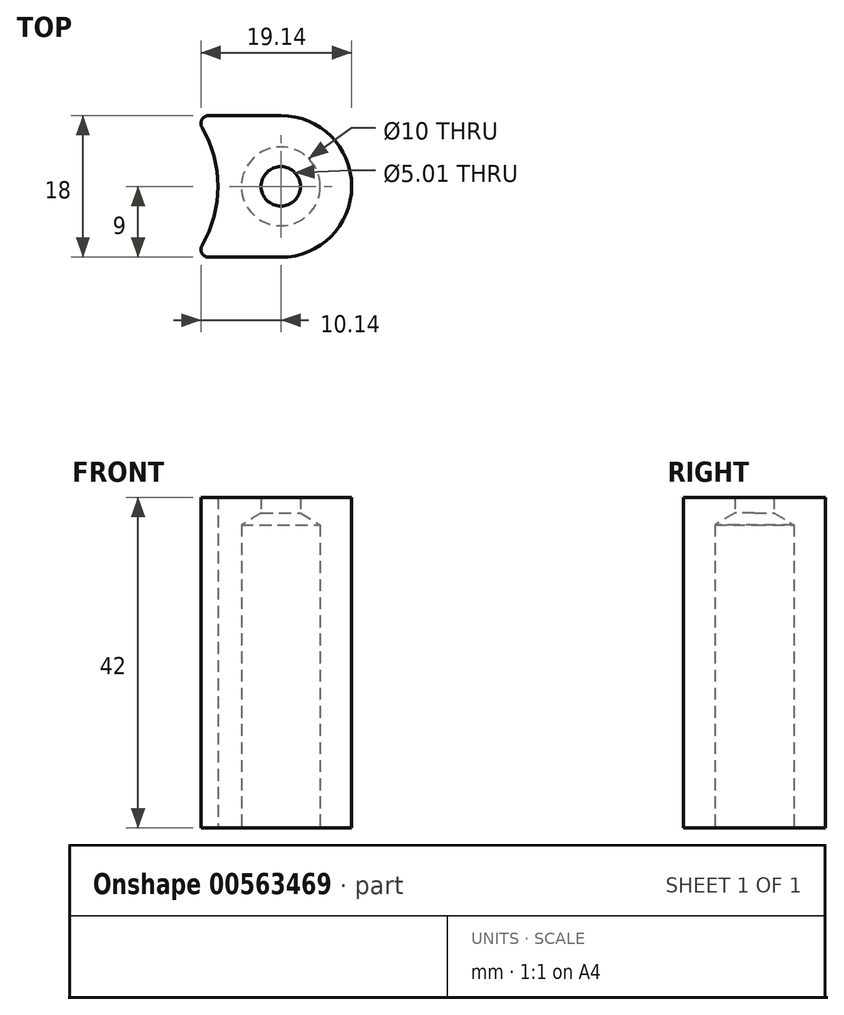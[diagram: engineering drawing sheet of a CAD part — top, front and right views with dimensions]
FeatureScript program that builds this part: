
annotation { "Feature Type Name" : "Feature", "Feature Type Description" : "" }
export const myFeature = defineFeature(function(context is Context, id is Id, definition is map)
    precondition{}
    {
        {
            var Q0;
            Q0=qCreatedBy(makeId("Top.planeOp"),FACE);
            var sketch = newSketch(context, id + "F0", { "sketchPlane" : qUnion([Q0])});
            skCircle(sketch, "E0", {"center": v(0, 0) * mm, "radius": 5 * mm});
            skCircle(sketch, "E1", {"center": v(0, 0) * mm, "radius": 9 * mm});
            skLineSegment(sketch, "E2.bottom", {"start": v(0, 9) * mm, "end": v(-11, 9) * mm});
            skLineSegment(sketch, "E2.top", {"start": v(0, -9) * mm, "end": v(-11, -9) * mm});
            skLineSegment(sketch, "E2.left", {"start": v(0, 9) * mm, "end": v(0, -9) * mm});
            skLineSegment(sketch, "E2.right", {"start": v(-11, 9) * mm, "end": v(-11, -9) * mm});
            skArc(sketch, "E3", {"start": v(-11, -9) * mm, "mid": v(-8, 0) * mm, "end": v(-11, 9) * mm});
            skSolve(sketch);
        }
        {
            var Q0;
            {var subQ0=sQuery(id+"F0.wireOp",EDGE,"E2.left");var subQ5=sQuery(id+"F0.wireOp",EDGE,"E0");var subQ6=makeQuery(id+"F0.imprint","INTERSECT",VERTEX,{"disambiguationData":[OD(0.0)],"derivedFrom":[subQ5,subQ0]});Q0=makeQuery(id+"F0.imprint","IMPRINT",FACE,{"disambiguationData":[TD([[makeQuery(id+"F0.imprint","IMPRINT",EDGE,{"disambiguationData":[TD([[subQ6,-1.0]])],"derivedFrom":subQ5}),-1.0]])]});}
            var Q1;
            {var subQ0=sQuery(id+"F0.wireOp",EDGE,"E2.bottom");Q1=makeQuery(id+"F0.imprint","IMPRINT",FACE,{"disambiguationData":[TD([[makeQuery(id+"F0.imprint","IMPRINT",EDGE,{"derivedFrom":subQ0}),1.0]])]});}
            var Q2;
            {var subQ0=sQuery(id+"F0.wireOp",EDGE,"E2.top");Q2=makeQuery(id+"F0.imprint","IMPRINT",FACE,{"disambiguationData":[TD([[makeQuery(id+"F0.imprint","IMPRINT",EDGE,{"derivedFrom":subQ0}),-1.0]])]});}
            var Q3;
            {var subQ0=sQuery(id+"F0.wireOp",EDGE,"E2.left");var subQ1=sQuery(id+"F0.wireOp",EDGE,"E0");var subQ2=makeQuery(id+"F0.imprint","INTERSECT",VERTEX,{"disambiguationData":[OD(0.0)],"derivedFrom":[subQ1,subQ0]});Q3=makeQuery(id+"F0.imprint","IMPRINT",FACE,{"disambiguationData":[TD([[makeQuery(id+"F0.imprint","IMPRINT",EDGE,{"disambiguationData":[TD([[subQ2,1.0]])],"derivedFrom":subQ1}),-1.0]])]});}
            var Q4;
            {var subQ0=sQuery(id+"F0.wireOp",EDGE,"E2.left");var subQ1=sQuery(id+"F0.wireOp",EDGE,"E0");var subQ2=makeQuery(id+"F0.imprint","INTERSECT",VERTEX,{"disambiguationData":[OD(0.0)],"derivedFrom":[subQ1,subQ0]});Q4=makeQuery(id+"F0.imprint","IMPRINT",FACE,{"disambiguationData":[TD([[makeQuery(id+"F0.imprint","IMPRINT",EDGE,{"disambiguationData":[TD([[subQ2,-1.0]])],"derivedFrom":subQ1}),1.0]])]});}
            var Q5;
            {var subQ0=sQuery(id+"F0.wireOp",EDGE,"E2.left");var subQ1=sQuery(id+"F0.wireOp",EDGE,"E0");var subQ2=makeQuery(id+"F0.imprint","INTERSECT",VERTEX,{"disambiguationData":[OD(0.0)],"derivedFrom":[subQ1,subQ0]});Q5=makeQuery(id+"F0.imprint","IMPRINT",FACE,{"disambiguationData":[TD([[makeQuery(id+"F0.imprint","IMPRINT",EDGE,{"disambiguationData":[TD([[subQ2,1.0]])],"derivedFrom":subQ1}),1.0]])]});}
            extrude(context, id + "F1", {"entities" : qUnion([Q0, Q1, Q2, Q3, Q4, Q5]), "depth" : 40 * mm, "offsetDistance" : 25 * mm});
        }
        {
            var Q0;
            Q0=makeQuery(id+"F1.opExtrude","CAP_FACE",FACE,{"disambiguationData":[OSD([sQuery(id+"F0.wireOp",EDGE,"E1"),sQuery(id+"F0.wireOp",EDGE,"E2.bottom"),sQuery(id+"F0.wireOp",EDGE,"E2.top"),sQuery(id+"F0.wireOp",EDGE,"E2.right")])],"isStart":true});
            var sketch = newSketch(context, id + "F2", { "sketchPlane" : qUnion([Q0])});
            skPoint(sketch, "E4", {"position": v(0, 0) * mm});
            skSolve(sketch);
        }
        {
            var Q0;
            Q0=sQuery(id+"F2.wireOp",VERTEX,"E4");
            var Q1;
            Q1=makeQuery(id+"F1.opExtrude","SWEPT_BODY",BODY,{"disambiguationData":[OSD([sQuery(id+"F0.wireOp",EDGE,"E1"),sQuery(id+"F0.wireOp",EDGE,"E2.bottom"),sQuery(id+"F0.wireOp",EDGE,"E2.top"),sQuery(id+"F0.wireOp",EDGE,"E2.right")])]});
            hole(context, id + "F3", {"style" : HoleStyle.SIMPLE, "endStyle" : HoleEndStyle.BLIND, "holeDiameter" : 10 * mm, "holeDepth" : 38.5 * mm, "isTappedThrough" : true, "tappedDepth" : 12 * mm, "tapClearance" : 3, "locations" : qUnion([Q0]), "scope" : qUnion([Q1])});
        }
        {
            var Q0;
            Q0=makeQuery(id+"F1.opExtrude","CAP_FACE",FACE,{"disambiguationData":[OSD([sQuery(id+"F0.wireOp",EDGE,"E1"),sQuery(id+"F0.wireOp",EDGE,"E2.bottom"),sQuery(id+"F0.wireOp",EDGE,"E2.top"),sQuery(id+"F0.wireOp",EDGE,"E2.right")])],"isStart":false});
            extrude(context, id + "F4", {"entities" : qUnion([Q0]), "operationType" : NewBodyOperationType.ADD, "depth" : 2 * mm, "offsetDistance" : 25 * mm});
        }
        {
            var Q0;
            {var subQ0=sQuery(id+"F0.wireOp",EDGE,"E3");var subQ1=sQuery(id+"F0.wireOp",EDGE,"E2.right");var subQ2=sQuery(id+"F0.wireOp",EDGE,"E2.top");Q0=makeQuery(id+"F4.boolean.opBoolean","MERGE",EDGE,{"derivedFrom":[makeQuery(id+"F1.opExtrude","SWEPT_EDGE",EDGE,{"disambiguationData":[OSD([subQ2,subQ1,subQ0])]}),makeQuery(id+"F4.opExtrude","SWEPT_EDGE",EDGE,{"disambiguationData":[OSD([subQ2,subQ1,subQ0])]})]});}
            var Q1;
            {var subQ0=sQuery(id+"F0.wireOp",EDGE,"E3");var subQ1=sQuery(id+"F0.wireOp",EDGE,"E2.right");var subQ2=sQuery(id+"F0.wireOp",EDGE,"E2.bottom");Q1=makeQuery(id+"F4.boolean.opBoolean","MERGE",EDGE,{"derivedFrom":[makeQuery(id+"F1.opExtrude","SWEPT_EDGE",EDGE,{"disambiguationData":[OSD([subQ2,subQ1,subQ0])]}),makeQuery(id+"F4.opExtrude","SWEPT_EDGE",EDGE,{"disambiguationData":[OSD([subQ2,subQ1,subQ0])]})]});}
            fillet(context, id + "F5", {"entities" : qUnion([Q0, Q1]), "radius" : 1 * mm, "tangentPropagation" : true, "allowEdgeOverflow" : false});
        }
    });
